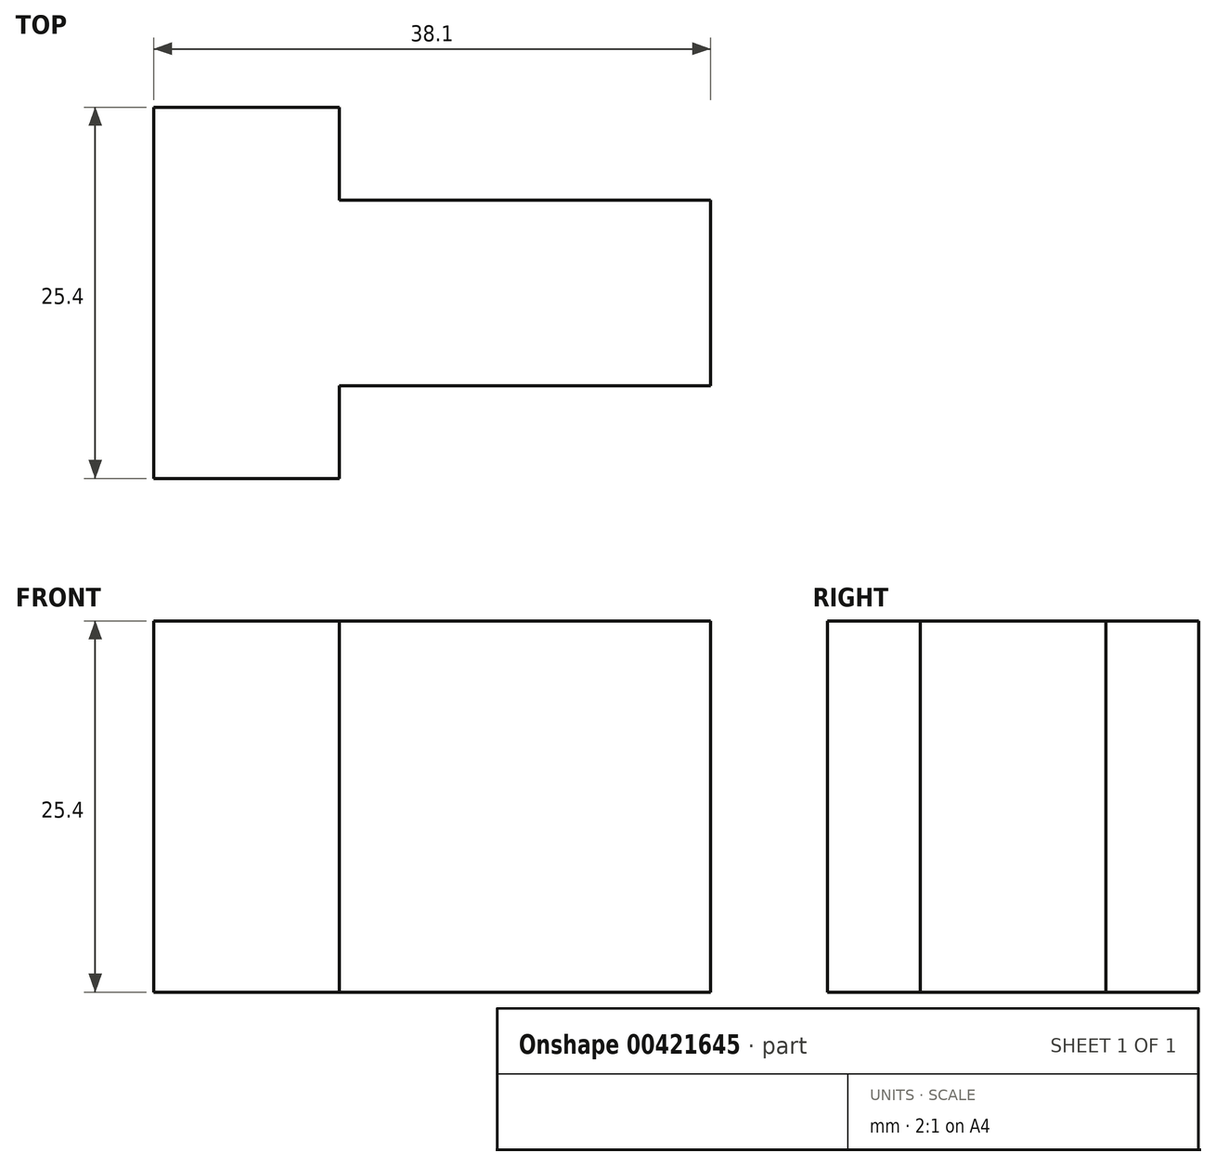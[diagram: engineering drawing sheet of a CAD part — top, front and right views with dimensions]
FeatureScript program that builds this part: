
annotation { "Feature Type Name" : "Feature", "Feature Type Description" : "" }
export const myFeature = defineFeature(function(context is Context, id is Id, definition is map)
    precondition{}
    {
        {
            var Q0;
            Q0=qCreatedBy(makeId("Top.planeOp"),FACE);
            var sketch = newSketch(context, id + "F0", { "sketchPlane" : qUnion([Q0])});
            skLineSegment(sketch, "E0", {"start": v(0, 0) * mm, "end": v(12.7, 0) * mm});
            skLineSegment(sketch, "E1", {"start": v(12.7, 0) * mm, "end": v(12.7, 6.35) * mm});
            skLineSegment(sketch, "E2", {"start": v(12.7, 6.35) * mm, "end": v(38.1, 6.35) * mm});
            skLineSegment(sketch, "E3", {"start": v(38.1, 6.35) * mm, "end": v(38.1, 19.05) * mm});
            skLineSegment(sketch, "E4", {"start": v(38.1, 19.05) * mm, "end": v(12.7, 19.05) * mm});
            skLineSegment(sketch, "E5", {"start": v(12.7, 19.05) * mm, "end": v(12.7, 25.4) * mm});
            skLineSegment(sketch, "E6", {"start": v(12.7, 25.4) * mm, "end": v(0, 25.4) * mm});
            skLineSegment(sketch, "E7", {"start": v(0, 25.4) * mm, "end": v(0, 0) * mm});
            skSolve(sketch);
        }
        {
            var Q0;
            Q0=makeQuery(id+"F0.imprint","IMPRINT",FACE,{"disambiguationData":[TD([[makeQuery(id+"F0.imprint","IMPRINT",EDGE,{"derivedFrom":sQuery(id+"F0.wireOp",EDGE,"E0")}),1.0]])]});
            extrude(context, id + "F1", {"entities" : qUnion([Q0]), "depth" : 25.4 * mm});
        }
    });
